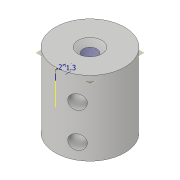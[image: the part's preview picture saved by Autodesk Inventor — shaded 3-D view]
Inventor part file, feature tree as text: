
AUTODESK INVENTOR PART (.ipt)
format: ipt  version: 2019.4 (Build 234330000, 330)  size: 164,864 bytes
history: native  units: mm
features: extrude x3, sketch x3, plane x1, pattern_circular x1, chamfer x1, pattern_linear x1
ambient origin geometry x8: Origin, YZ Plane, XZ Plane, XY Plane, X Axis, Y Axis, Z Axis, Center Point
bodies: Solid1 (feature_tree)
feature tree (10):
  extrude  "Extrusion1"  Depth=7.0mm TaperAngle=0.0deg
  extrude  "Extrusion2"  Depth=2.2mm
  plane  "Work Plane1"
  sketch  "Sketch5"  dims[d4=5.1mm d5=2.2mm]
  extrude  "Extrusion5"  [1 undecoded]
  pattern_circular  "Circular Pattern3"  [2 undecoded]
  chamfer  "Chamfer4"  Distance=2.0mm
  pattern_linear  "Rectangular Pattern2"  Spacing1=2.8mm  [1 undecoded]
  sketch  "Sketch2"  dims[d0=14.0mm d2=7.0mm d3=0.0mm]
  sketch  "Sketch6"  dims[d6=8.0mm d7=0.0mm d14=-6.0mm d17=1.3mm d18=2.0mm d42=2.8mm d43=2.9mm d44=7.0mm d45=10.0mm d46=0.0mm d47=30.0mm d48=360.0deg d50=1.0mm d51=2.0mm d52=45.0deg d53=20.0mm d55=7.0mm]
note: 4 required parameter values undecoded (feature->parameter linkage not recoverable at this tier; creation-order binding heuristic only, values carry confidence <= 0.55)
